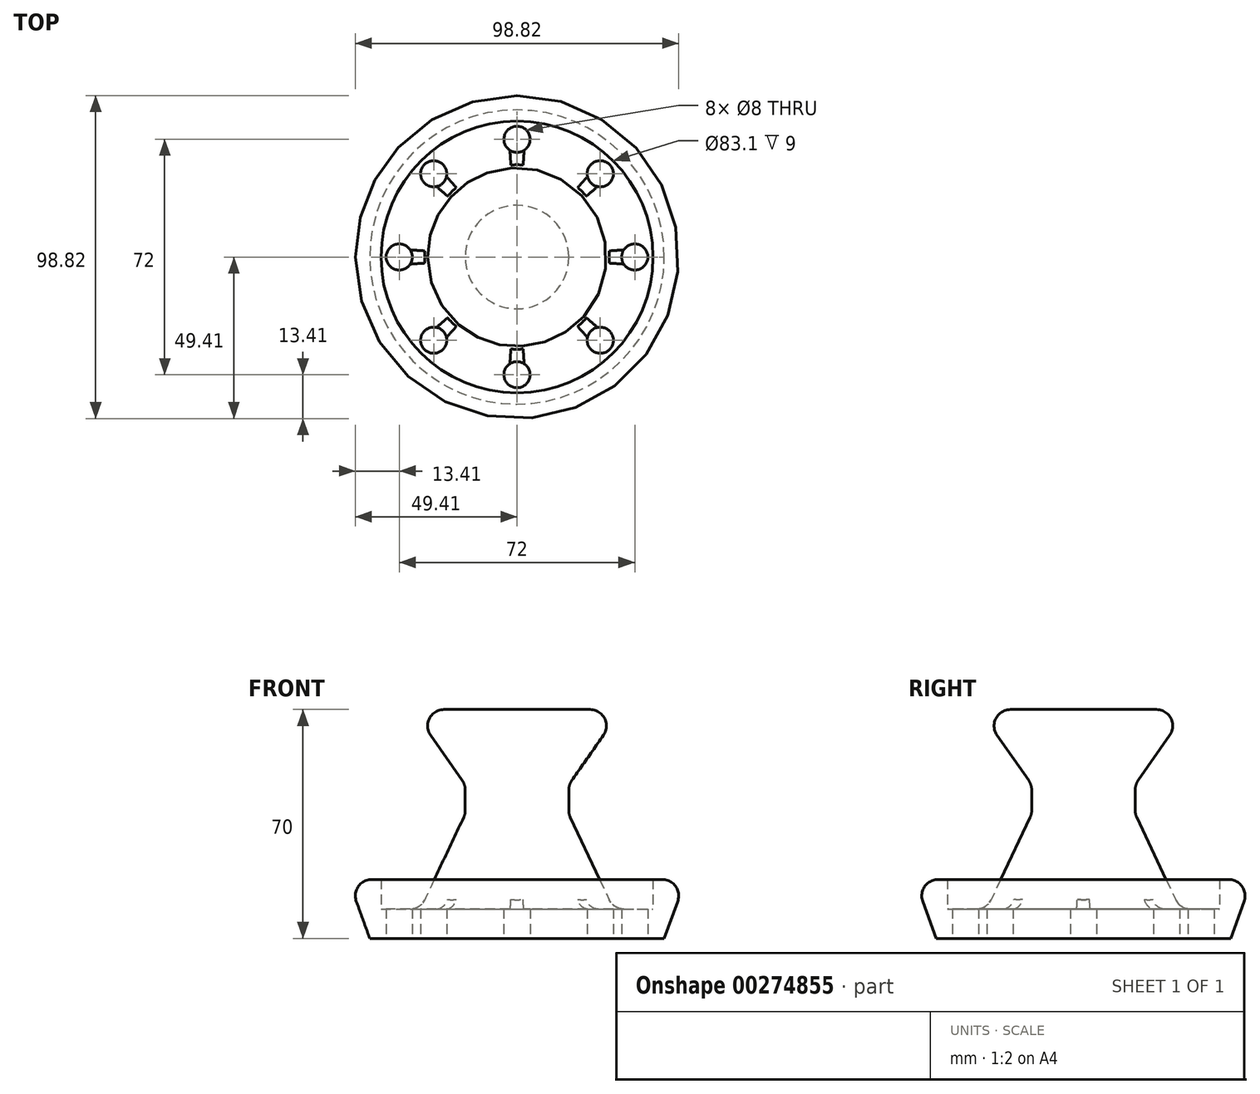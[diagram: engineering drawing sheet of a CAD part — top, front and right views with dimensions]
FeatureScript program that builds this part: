
annotation { "Feature Type Name" : "Feature", "Feature Type Description" : "" }
export const myFeature = defineFeature(function(context is Context, id is Id, definition is map)
    precondition{}
    {
        {
            var Q0;
            Q0=qCreatedBy(makeId("Front.planeOp"),FACE);
            var sketch = newSketch(context, id + "F0", { "sketchPlane" : qUnion([Q0])});
            skLineSegment(sketch, "E0", {"start": v(0, 0) * mm, "end": v(0, 70) * mm});
            skLineSegment(sketch, "E1", {"start": v(0, 70) * mm, "end": v(-31.93, 70) * mm});
            skLineSegment(sketch, "E2", {"start": v(-31.93, 70) * mm, "end": v(-15.82, 47) * mm});
            skLineSegment(sketch, "E3", {"start": v(-15.82, 47) * mm, "end": v(-15.82, 38) * mm});
            skLineSegment(sketch, "E4", {"start": v(-15.82, 38) * mm, "end": v(-29.55, 9) * mm});
            skLineSegment(sketch, "E5", {"start": v(-29.55, 9) * mm, "end": v(-41.55, 9) * mm});
            skLineSegment(sketch, "E6", {"start": v(-41.55, 9) * mm, "end": v(-41.55, 18) * mm});
            skLineSegment(sketch, "E7", {"start": v(-41.55, 18) * mm, "end": v(-51.55, 18) * mm});
            skLineSegment(sketch, "E8", {"start": v(-51.55, 18) * mm, "end": v(-45, 0) * mm});
            skLineSegment(sketch, "E9", {"start": v(-45, 0) * mm, "end": v(0, 0) * mm});
            skSolve(sketch);
        }
        {
            var Q0;
            Q0 = qSketchRegion(id + "F0", true);
            var Q1;
            Q1=sQuery(id+"F0.wireOp",EDGE,"E0");
            revolve(context, id + "F1", {"entities" : qUnion([Q0]), "axis" : qUnion([Q1]), "revolveType" : RevolveType.FULL});
        }
        {
            var Q0;
            Q0=makeQuery(id+"F1.opRevolve","SWEPT_FACE",FACE,{"disambiguationData":[OSD([sQuery(id+"F0.wireOp",EDGE,"E9")])]});
            var sketch = newSketch(context, id + "F2", { "sketchPlane" : qUnion([Q0])});
            skCircle(sketch, "E10", {"center": v(-36, 0) * mm, "radius": 4 * mm});
            skCircle(sketch, "E11.1.0", {"center": v(-25.46, -25.46) * mm, "radius": 4 * mm});
            skCircle(sketch, "E11.2.0", {"center": v(0, -36) * mm, "radius": 4 * mm});
            skCircle(sketch, "E11.3.0", {"center": v(25.46, -25.46) * mm, "radius": 4 * mm});
            skCircle(sketch, "E11.4.0", {"center": v(36, 0) * mm, "radius": 4 * mm});
            skCircle(sketch, "E11.5.0", {"center": v(25.46, 25.46) * mm, "radius": 4 * mm});
            skCircle(sketch, "E11.6.0", {"center": v(0, 36) * mm, "radius": 4 * mm});
            skCircle(sketch, "E11.7.0", {"center": v(-25.46, 25.46) * mm, "radius": 4 * mm});
            skPoint(sketch, "E11.center", {"position": v(0, 0) * mm});
            skSolve(sketch);
        }
        {
            var Q0;
            Q0 = qSketchRegion(id + "F2", true);
            extrude(context, id + "F3", {"entities" : qUnion([Q0]), "operationType" : NewBodyOperationType.REMOVE, "endBound" : BoundingType.THROUGH_ALL, "oppositeDirection" : true, "depth" : 25 * mm});
        }
        {
            var Q0;
            Q0=makeQuery(id+"F1.opRevolve","SWEPT_EDGE",EDGE,{"disambiguationData":[OSD([sQuery(id+"F0.wireOp",EDGE,"E1"),sQuery(id+"F0.wireOp",EDGE,"E2")])]});
            var Q1;
            Q1=makeQuery(id+"F1.opRevolve","SWEPT_EDGE",EDGE,{"disambiguationData":[OSD([sQuery(id+"F0.wireOp",EDGE,"E7"),sQuery(id+"F0.wireOp",EDGE,"E8")])]});
            var Q2;
            Q2=makeQuery(id+"F1.opRevolve","SWEPT_EDGE",EDGE,{"disambiguationData":[OSD([sQuery(id+"F0.wireOp",EDGE,"E2"),sQuery(id+"F0.wireOp",EDGE,"E3")])]});
            var Q3;
            Q3=makeQuery(id+"F1.opRevolve","SWEPT_EDGE",EDGE,{"disambiguationData":[OSD([sQuery(id+"F0.wireOp",EDGE,"E3"),sQuery(id+"F0.wireOp",EDGE,"E4")])]});
            var Q4;
            Q4=makeQuery(id+"F1.opRevolve","SWEPT_EDGE",EDGE,{"disambiguationData":[OSD([sQuery(id+"F0.wireOp",EDGE,"E4"),sQuery(id+"F0.wireOp",EDGE,"E5")])]});
            fillet(context, id + "F4", {"entities" : qUnion([Q0, Q1, Q2, Q3, Q4]), "radius" : 5 * mm, "tangentPropagation" : true, "allowEdgeOverflow" : false});
        }
    });
